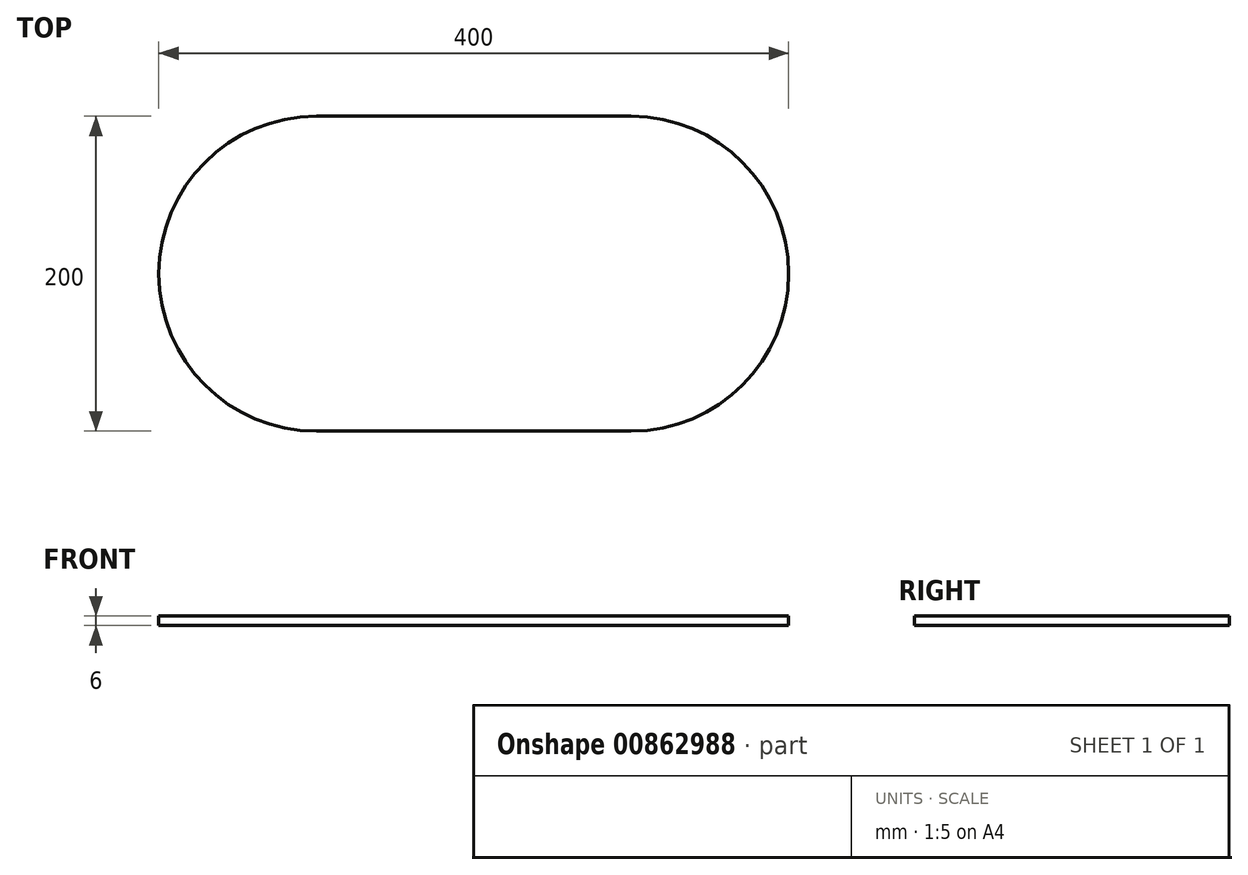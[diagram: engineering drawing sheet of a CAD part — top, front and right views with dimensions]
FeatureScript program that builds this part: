
annotation { "Feature Type Name" : "Feature", "Feature Type Description" : "" }
export const myFeature = defineFeature(function(context is Context, id is Id, definition is map)
    precondition{}
    {
        {
            var Q0;
            Q0=qCreatedBy(makeId("Top.planeOp"),FACE);
            var sketch = newSketch(context, id + "F0", { "sketchPlane" : qUnion([Q0])});
            skLineSegment(sketch, "E0.bottom", {"start": v(200, -100) * mm, "end": v(-200, -100) * mm});
            skLineSegment(sketch, "E0.top", {"start": v(200, 100) * mm, "end": v(-200, 100) * mm});
            skLineSegment(sketch, "E0.left", {"start": v(200, -100) * mm, "end": v(200, 100) * mm});
            skLineSegment(sketch, "E0.right", {"start": v(-200, -100) * mm, "end": v(-200, 100) * mm});
            skPoint(sketch, "E0.middle", {"position": v(0, 0) * mm});
            skSolve(sketch);
        }
        {
            var Q0;
            Q0 = qSketchRegion(id + "F0", true);
            extrude(context, id + "F1", {"entities" : qUnion([Q0]), "flatOperationType" : FlatOperationType.REMOVE, "depth" : 6 * mm, "offsetDistance" : 25 * mm, "domain" : OperationDomain.MODEL, "symmetric" : true});
        }
        {
            var Q0;
            Q0=makeQuery(id+"F1.opExtrude","SWEPT_EDGE",EDGE,{"disambiguationData":[OSD([sQuery(id+"F0.wireOp",EDGE,"E0.top"),sQuery(id+"F0.wireOp",EDGE,"E0.right")])]});
            var Q1;
            Q1=makeQuery(id+"F1.opExtrude","SWEPT_EDGE",EDGE,{"disambiguationData":[OSD([sQuery(id+"F0.wireOp",EDGE,"E0.bottom"),sQuery(id+"F0.wireOp",EDGE,"E0.right")])]});
            var Q2;
            Q2=makeQuery(id+"F1.opExtrude","SWEPT_EDGE",EDGE,{"disambiguationData":[OSD([sQuery(id+"F0.wireOp",EDGE,"E0.bottom"),sQuery(id+"F0.wireOp",EDGE,"E0.left")])]});
            var Q3;
            Q3=makeQuery(id+"F1.opExtrude","SWEPT_EDGE",EDGE,{"disambiguationData":[OSD([sQuery(id+"F0.wireOp",EDGE,"E0.top"),sQuery(id+"F0.wireOp",EDGE,"E0.left")])]});
            fillet(context, id + "F2", {"entities" : qUnion([Q0, Q1, Q2, Q3]), "tangentPropagation" : true, "radius" : 100 * mm, "defaultsChanged" : true, "vertexSettings" : [], "allowEdgeOverflow" : false});
        }
    });
